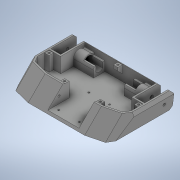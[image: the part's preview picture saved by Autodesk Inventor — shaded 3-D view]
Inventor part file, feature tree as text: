
AUTODESK INVENTOR PART (.ipt)
format: ipt  version: 2020 (Build 240168000, 168)  size: 651,264 bytes
history: native  units: mm
features: extrude x19, sketch x19, projected_geometry x9, chamfer x6, plane x3, mirror x2
ambient origin geometry x8: Origin, YZ Plane, XZ Plane, XY Plane, X Axis, Y Axis, Z Axis, Center Point
bodies: Solid1 (feature_tree)
feature tree (58):
  extrude  "Extrusion1"  Depth=120.0mm
  extrude  "Extrusion2"  TaperAngle=0.0deg  [1 undecoded]
  plane  "Work Plane2"
  extrude  "Extrusion6"  Depth=10.0mm
  plane  "Work Plane4"
  plane  "Work Plane5"
  extrude  "Extrusion7"  TaperAngle=0.0deg  [1 undecoded]
  extrude  "Extrusion8"  Depth=83.204mm TaperAngle=0.0deg
  chamfer  "Chamfer1"  Distance=20.747mm
  chamfer  "Chamfer2"  Distance=27.254mm
  chamfer  "Chamfer3"  Distance=2.0mm Angle=45.0deg
  chamfer  "Chamfer4"  Distance=6.0mm Angle=45.0deg
  chamfer  "Chamfer6"  [1 undecoded]
  extrude  "Extrusion9"  TaperAngle=0.0deg  [1 undecoded]
  extrude  "Extrusion10"  Depth=6.0mm
  extrude  "Extrusion11"  Depth=8.0mm
  extrude  "Extrusion12"  Depth=8.0mm
  mirror  "Mirror2"
  extrude  "WeaponMountSlot"  Depth=8.0mm
  chamfer  "Chamfer7"  Distance=157.438mm
  extrude  "Extrusion14"  Depth=8.0mm
  extrude  "Extrusion15"  Depth=8.0mm TaperAngle=0.0deg
  extrude  "Extrusion16"  Depth=10.0mm TaperAngle=0.0deg
  extrude  "Extrusion17"  Depth=8.0mm
  extrude  "WeaponMountHoles"  Depth=55.8mm
  extrude  "Extrusion19"  Depth=2.0mm TaperAngle=45.0deg
  extrude  "Extrusion20"  Depth=8.0mm
  extrude  "Extrusion21"  Depth=26.0mm
  mirror  "Mirror3"
  extrude  "Extrusion22"  TaperAngle=0.0deg  [1 undecoded]
  sketch  "Sketch1"  dims[d0=180.0mm d1=120.0mm]
  sketch  "Sketch3"  dims[d2=30.0mm d3=0.0mm]
  sketch  "Sketch7"  dims[d4=100.8mm d5=10.0mm]
  projected_geometry  "Projected Loop3"
  sketch  "Sketch9"  dims[d6=10.0mm d7=0.0mm d8=0.0mm]
  sketch  "Sketch10"  dims[d10=45.0deg d18=83.204mm d19=0.0mm d20=20.747mm d21=0.0mm d22=27.254mm d23=0.0mm]
  sketch  "Sketch11"  dims[d24=10.0mm d25=2.0mm d26=45.0deg]
  projected_geometry  "Projected Loop4"
  sketch  "Sketch12"  dims[d27=3.0mm d28=6.0mm d29=45.0deg]
  projected_geometry  "Projected Loop8"
  sketch  "Sketch16"  dims[d30=24.0mm]
  sketch  "Sketch17"  dims[d31=3.0mm]
  sketch  "Sketch18"  dims[d32=45.0deg]
  sketch  "Sketch19"  dims[d33=3.0mm]
  sketch  "Sketch20"  dims[d34=6.0mm]
  projected_geometry  "Projected Loop9"
  projected_geometry  "Projected Loop10"
  projected_geometry  "Projected Loop11"
  projected_geometry  "Projected Loop12"
  sketch  "Sketch21"  dims[d35=45.0deg]
  sketch  "Sketch22"  dims[d39=24.0mm]
  sketch  "Sketch23"  dims[d40=3.0mm]
  sketch  "Sketch24"  dims[d41=45.0deg]
  sketch  "Sketch25"  dims[d45=17.7mm]
  sketch  "Sketch26"  dims[d46=46.15mm d47=0.0mm d48=0.0mm]
  projected_geometry  "Projected Loop13"
  sketch  "Sketch27"  dims[d52=27.0mm d53=0.0mm d58=6.0mm d64=6.5mm d65=16.15mm d66=15.0mm d67=157.438mm d68=0.0mm d69=4.5mm d70=173.156mm d71=0.0mm d72=10.0mm d73=0.0mm d75=37.4mm d76=55.8mm d77=5.0mm d78=2.0mm d79=45.0deg d80=8.0mm d81=26.0mm d82=0.0mm d83=3.75mm d84=3.75mm d85=3.75mm d86=3.75mm d87=7.0mm d88=0.0mm d90=6.0mm d91=4.0mm d92=15.0mm d93=23.0mm d94=7.0mm d95=0.0mm d96=4.0mm d97=15.0mm d98=23.0mm d99=7.0mm d100=0.0mm d101=3.0mm d102=60.0mm d103=3.1mm d104=3.1mm d105=3.1mm d106=3.1mm d107=10.0mm d108=9.4mm d109=9.4mm d110=64.0mm d111=64.0mm d112=9.4mm d113=9.4mm d114=10.0mm d115=27.0mm d116=0.0mm d117=6.1mm d118=0.0mm d119=-7.853982mm d120=16.3mm d121=16.15mm d122=15.0mm d123=2.0mm d124=20.3mm d125=17.0mm d126=0.0mm d127=15.5mm d128=12.2mm d129=19.0mm d130=0.0mm d131=45.0deg d133=19.0mm d134=0.0mm d135=8.0mm d137=6.1mm]
  projected_geometry  "Projected Loop14"
note: 5 required parameter values undecoded (feature->parameter linkage not recoverable at this tier; creation-order binding heuristic only, values carry confidence <= 0.55)
